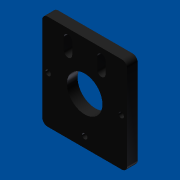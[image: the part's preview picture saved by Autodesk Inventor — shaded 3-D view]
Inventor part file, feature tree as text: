
AUTODESK INVENTOR PART (.ipt)
format: ipt  version: 2012 SP1 (Build 160190100, 190)  size: 132,608 bytes
history: native  units: mm (DEFAULTED — no unit token found)
features: extrude x4, sketch x4, pattern_linear x1, fillet x1
ambient origin geometry x8: Origin, YZ Plane, XZ Plane, XY Plane, X Axis, Y Axis, Z Axis, Center Point
bodies: Solid1 (feature_tree)
feature tree (10):
  extrude  "Extrusion4"  Depth=57.15mm
  extrude  "Extrusion5"  Depth=21.25mm
  extrude  "Extrusion6"  Depth=29.05mm
  extrude  "Extrusion7"  Depth=3.5mm
  pattern_linear  "Rectangular Pattern1"  Spacing1=3.2004mm  [1 undecoded]
  fillet  "Fillet1"  Radius=3.49mm
  sketch  "Sketch1"  dims[d25=50.8mm d26=57.15mm]
  sketch  "Sketch3"  dims[d27=6.35mm d28=0.0mm d29=21.25mm]
  sketch  "Sketch4"  dims[d30=25.4mm d31=29.05mm]
  sketch  "Sketch5"  dims[d32=6.35mm d33=0.0mm d36=3.5mm d37=3.2004mm d38=3.49mm d39=29.05mm d40=3.2004mm d41=47.32mm d42=29.05mm d43=3.2004mm d44=25.4mm d45=50.96mm d46=6.35mm d47=0.0mm d48=5.0mm d49=5.0mm d51=12.7mm d53=15.4mm d54=6.35mm d55=0.0mm d62=7.0mm d63=7.0mm d64=5.0mm d65=20.0mm d67=20.0mm d68=3.175mm]
note: 1 required parameter value undecoded (feature->parameter linkage not recoverable at this tier; creation-order binding heuristic only, values carry confidence <= 0.55)
